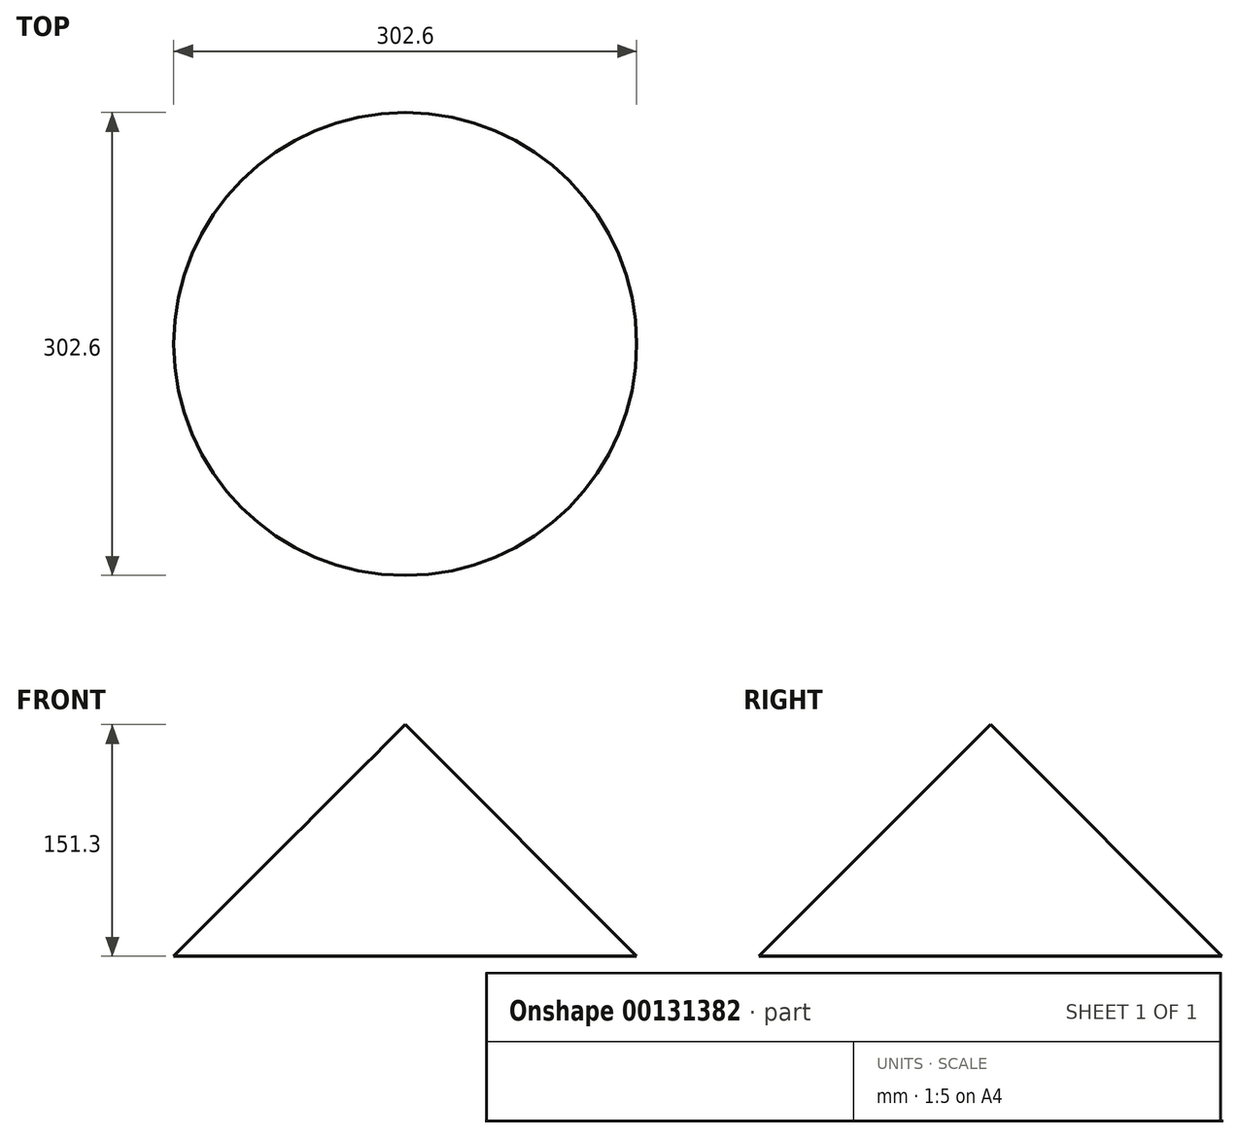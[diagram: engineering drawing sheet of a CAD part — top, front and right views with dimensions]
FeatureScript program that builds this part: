
annotation { "Feature Type Name" : "Feature", "Feature Type Description" : "" }
export const myFeature = defineFeature(function(context is Context, id is Id, definition is map)
    precondition{}
    {
        {
            var Q0;
            Q0=qCreatedBy(makeId("Front.planeOp"),FACE);
            var sketch = newSketch(context, id + "F0", { "sketchPlane" : qUnion([Q0])});
            skLineSegment(sketch, "E0", {"start": v(-75.8, 78.02) * mm, "end": v(-75.8, -73.28) * mm});
            skLineSegment(sketch, "E1", {"start": v(-75.8, -73.28) * mm, "end": v(75.5, -73.28) * mm});
            skLineSegment(sketch, "E2", {"start": v(75.5, -73.28) * mm, "end": v(-75.8, 78.02) * mm});
            skSolve(sketch);
        }
        {
            var Q0;
            Q0=makeQuery(id+"F0.imprint","IMPRINT",FACE,{"disambiguationData":[TD([[makeQuery(id+"F0.imprint","IMPRINT",EDGE,{"derivedFrom":sQuery(id+"F0.wireOp",EDGE,"E0")}),1.0]])]});
            var Q1;
            Q1=sQuery(id+"F0.wireOp",EDGE,"E0");
            revolve(context, id + "F1", {"entities" : qUnion([Q0]), "axis" : qUnion([Q1]), "revolveType" : RevolveType.FULL});
        }
    });
